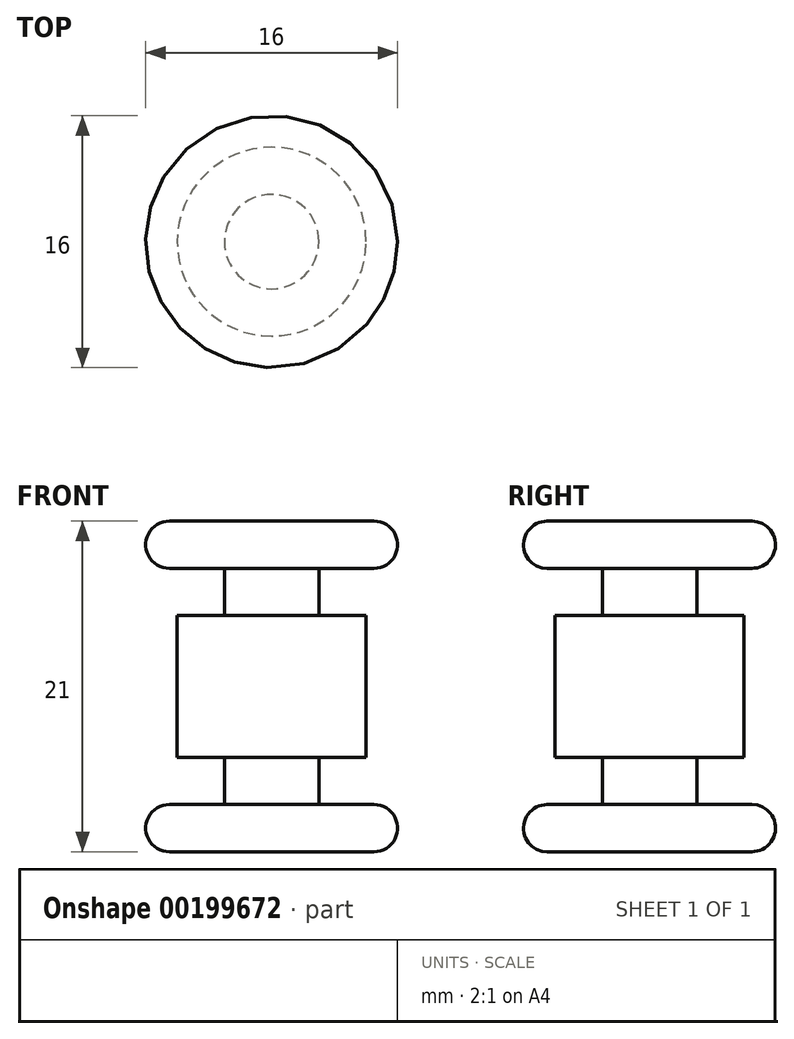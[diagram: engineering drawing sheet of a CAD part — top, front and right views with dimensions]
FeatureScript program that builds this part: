
annotation { "Feature Type Name" : "Feature", "Feature Type Description" : "" }
export const myFeature = defineFeature(function(context is Context, id is Id, definition is map)
    precondition{}
    {
        {
            var Q0;
            Q0=qCreatedBy(makeId("Top.planeOp"),FACE);
            var sketch = newSketch(context, id + "F0", { "sketchPlane" : qUnion([Q0])});
            skCircle(sketch, "E0", {"center": v(0, 0) * mm, "radius": 8 * mm});
            skSolve(sketch);
        }
        {
            var Q0;
            Q0=makeQuery(id+"F0.imprint","IMPRINT",FACE,{"disambiguationData":[TD([[makeQuery(id+"F0.imprint","IMPRINT",EDGE,{"derivedFrom":sQuery(id+"F0.wireOp",EDGE,"E0")}),1.0]])]});
            extrude(context, id + "F1", {"entities" : qUnion([Q0]), "depth" : 3 * mm});
        }
        {
            var Q0;
            Q0=makeQuery(id+"F1.opExtrude","CAP_FACE",FACE,{"disambiguationData":[OSD([sQuery(id+"F0.wireOp",EDGE,"E0")])],"isStart":false});
            var sketch = newSketch(context, id + "F2", { "sketchPlane" : qUnion([Q0])});
            skCircle(sketch, "E1", {"center": v(0, 0) * mm, "radius": 6 * mm});
            skSolve(sketch);
        }
        {
            var Q0;
            Q0=makeQuery(id+"F2.imprint","IMPRINT",FACE,{"disambiguationData":[TD([[makeQuery(id+"F2.imprint","IMPRINT",EDGE,{"derivedFrom":sQuery(id+"F2.wireOp",EDGE,"E1")}),1.0]])]});
            extrude(context, id + "F3", {"entities" : qUnion([Q0]), "operationType" : NewBodyOperationType.ADD, "depth" : 15 * mm});
        }
        {
            var Q0;
            Q0=makeQuery(id+"F3.opExtrude","CAP_FACE",FACE,{"disambiguationData":[OSD([sQuery(id+"F2.wireOp",EDGE,"E1")])],"isStart":false});
            var sketch = newSketch(context, id + "F4", { "sketchPlane" : qUnion([Q0])});
            skCircle(sketch, "E2", {"center": v(0, 0) * mm, "radius": 8 * mm});
            skSolve(sketch);
        }
        {
            var Q0;
            Q0=makeQuery(id+"F4.imprint","IMPRINT",FACE,{"disambiguationData":[TD([[makeQuery(id+"F4.imprint","IMPRINT",EDGE,{"derivedFrom":makeQuery(id+"F3.opExtrude","CAP_EDGE",EDGE,{"disambiguationData":[OSD([sQuery(id+"F2.wireOp",EDGE,"E1")])],"isStart":false})}),1.0]])]});
            var Q1;
            Q1=makeQuery(id+"F4.imprint","IMPRINT",FACE,{"disambiguationData":[TD([[makeQuery(id+"F4.imprint","IMPRINT",EDGE,{"derivedFrom":sQuery(id+"F4.wireOp",EDGE,"E2")}),1.0]])]});
            extrude(context, id + "F5", {"entities" : qUnion([Q0, Q1]), "operationType" : NewBodyOperationType.ADD, "depth" : 3 * mm});
        }
        {
            var Q0;
            Q0=makeQuery(id+"F5.opExtrude","CAP_EDGE",EDGE,{"disambiguationData":[OSD([sQuery(id+"F4.wireOp",EDGE,"E2")])],"isStart":false});
            var Q1;
            Q1=makeQuery(id+"F5.opExtrude","CAP_EDGE",EDGE,{"disambiguationData":[OSD([sQuery(id+"F4.wireOp",EDGE,"E2")])],"isStart":true});
            var Q2;
            Q2=makeQuery(id+"F1.opExtrude","CAP_EDGE",EDGE,{"disambiguationData":[OSD([sQuery(id+"F0.wireOp",EDGE,"E0")])],"isStart":false});
            var Q3;
            Q3=makeQuery(id+"F1.opExtrude","CAP_EDGE",EDGE,{"disambiguationData":[OSD([sQuery(id+"F0.wireOp",EDGE,"E0")])],"isStart":true});
            fillet(context, id + "F6", {"entities" : qUnion([Q0, Q1, Q2, Q3]), "radius" : 1.5 * mm, "tangentPropagation" : true, "allowEdgeOverflow" : false});
        }
        {
            var Q0;
            Q0=qCreatedBy(makeId("Front.planeOp"),FACE);
            var sketch = newSketch(context, id + "F7", { "sketchPlane" : qUnion([Q0])});
            skPoint(sketch, "E3.oppositeSnap0", {"position": v(0, 3) * mm});
            skPoint(sketch, "E3.oppositeSnap1", {"position": v(3, 6) * mm});
            skLineSegment(sketch, "E3.bottom", {"start": v(6, 6) * mm, "end": v(3, 6) * mm});
            skLineSegment(sketch, "E3.top", {"start": v(6, 3) * mm, "end": v(3, 3) * mm});
            skLineSegment(sketch, "E3.left", {"start": v(6, 6) * mm, "end": v(6, 3) * mm});
            skLineSegment(sketch, "E3.right", {"start": v(3, 6) * mm, "end": v(3, 3) * mm});
            skLineSegment(sketch, "E4.bottom", {"start": v(6, 15) * mm, "end": v(3, 15) * mm});
            skLineSegment(sketch, "E4.top", {"start": v(6, 18) * mm, "end": v(3, 18) * mm});
            skLineSegment(sketch, "E4.left", {"start": v(6, 15) * mm, "end": v(6, 18) * mm});
            skLineSegment(sketch, "E4.right", {"start": v(3, 15) * mm, "end": v(3, 18) * mm});
            skLineSegment(sketch, "E5", {"start": v(0, 0) * mm, "end": v(0, 23.5) * mm});
            skSolve(sketch);
        }
        {
            var Q0;
            Q0 = qSketchRegion(id + "F7", true);
            var Q1;
            Q1=sQuery(id+"F7.wireOp",EDGE,"E5");
            revolve(context, id + "F8", {"operationType" : NewBodyOperationType.REMOVE, "entities" : qUnion([Q0]), "axis" : qUnion([Q1]), "revolveType" : RevolveType.FULL, "oppositeDirection" : true});
        }
    });
